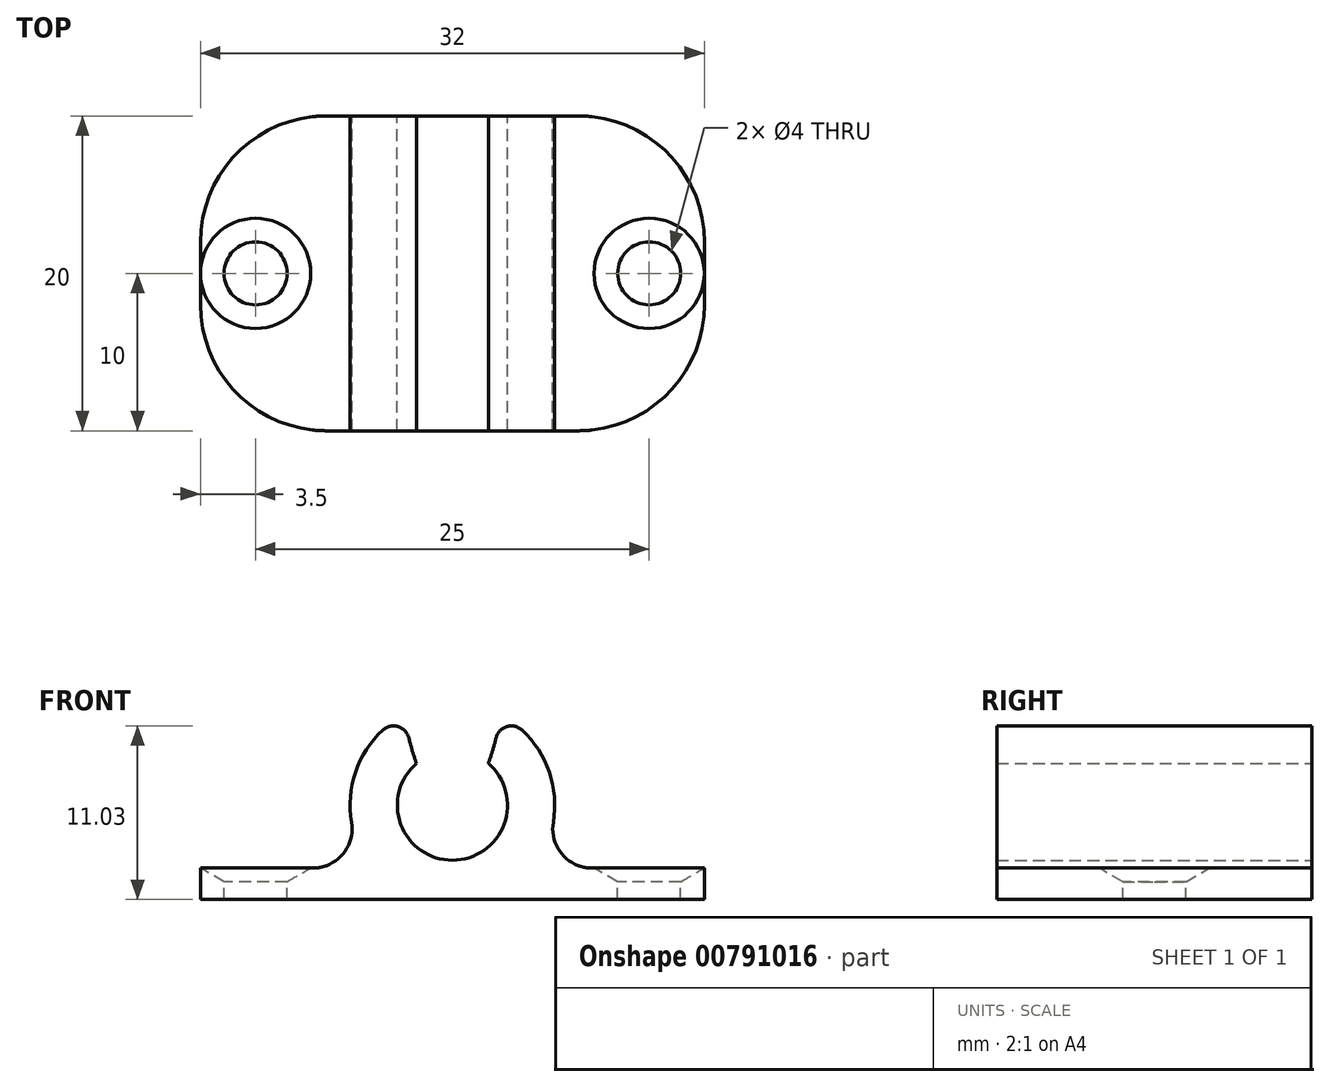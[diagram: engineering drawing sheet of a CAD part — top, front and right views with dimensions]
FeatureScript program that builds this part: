
annotation { "Feature Type Name" : "Feature", "Feature Type Description" : "" }
export const myFeature = defineFeature(function(context is Context, id is Id, definition is map)
    precondition{}
    {
        {
            var Q0;
            Q0=qCreatedBy(makeId("Front.planeOp"),FACE);
            var sketch = newSketch(context, id + "F0", { "sketchPlane" : qUnion([Q0])});
            skLineSegment(sketch, "E0.bottom", {"start": v(-16, 0) * mm, "end": v(16, 0) * mm});
            skLineSegment(sketch, "E0.top", {"start": v(-16, 2) * mm, "end": v(-8.87, 2) * mm});
            skLineSegment(sketch, "E0.left", {"start": v(-16, 0) * mm, "end": v(-16, 2) * mm});
            skLineSegment(sketch, "E0.right", {"start": v(16, 0) * mm, "end": v(16, 2) * mm});
            skArc(sketch, "E1", {"start": v(-2.28, 8.66) * mm, "mid": v(0, 2.5) * mm, "end": v(2.28, 8.66) * mm});
            skArc(sketch, "E2", {"start": v(-3.07, 11.73) * mm, "mid": v(-5.84, 8.86) * mm, "end": v(-6.4, 4.92) * mm});
            skArc(sketch, "E3", {"start": v(6.4, 4.92) * mm, "mid": v(6.96, 2.89) * mm, "end": v(8.87, 2) * mm});
            skArc(sketch, "E4", {"start": v(-8.87, 2) * mm, "mid": v(-6.96, 2.89) * mm, "end": v(-6.4, 4.92) * mm});
            skEllipticalArc(sketch, "E5", {});
            skEllipticalArc(sketch, "E6.trimOffspring", {});
            skArc(sketch, "E7.trimOffspring", {"start": v(6.4, 4.92) * mm, "mid": v(5.84, 8.86) * mm, "end": v(3.07, 11.73) * mm});
            skLineSegment(sketch, "E8.trimOffspring", {"start": v(8.87, 2) * mm, "end": v(16, 2) * mm});
            const initialGuessF0  = {"E5": [0, 0.016997944563627243, 0, -1, 0.010997944563627243, 0.0035, 5.212081421117064, 5.573529930797932], "E6.trimOffspring": [0, 0.016997944563627243, 0, -1, 0.010997944563627243, 0.0035, 0.7096553763816549, 1.0711038860625215]};
            skSetInitialGuess(sketch, initialGuessF0);
            skSolve(sketch);
        }
        {
            var Q0;
            Q0=makeQuery(id+"F0.imprint","IMPRINT",FACE,{"disambiguationData":[TD([[makeQuery(id+"F0.imprint","IMPRINT",EDGE,{"derivedFrom":sQuery(id+"F0.wireOp",EDGE,"E0.bottom")}),1.0]])]});
            extrude(context, id + "F1", {"entities" : qUnion([Q0]), "flatOperationType" : FlatOperationType.REMOVE, "depth" : 20 * mm, "offsetDistance" : 25 * mm, "domain" : OperationDomain.MODEL});
        }
        {
            var Q0;
            Q0=makeQuery(id+"F1.opExtrude","SWEPT_EDGE",EDGE,{"disambiguationData":[OSD([sQuery(id+"F0.wireOp",EDGE,"E2"),sQuery(id+"F0.wireOp",EDGE,"E5")])]});
            var Q1;
            Q1=makeQuery(id+"F1.opExtrude","SWEPT_EDGE",EDGE,{"disambiguationData":[OSD([sQuery(id+"F0.wireOp",EDGE,"E6.trimOffspring"),sQuery(id+"F0.wireOp",EDGE,"E7.trimOffspring")])]});
            fillet(context, id + "F2", {"entities" : qUnion([Q0, Q1]), "radius" : 1 * mm, "tangentPropagation" : true, "allowEdgeOverflow" : false});
        }
        {
            var Q0;
            Q0=makeQuery(id+"F1.opExtrude","CAP_EDGE",EDGE,{"disambiguationData":[OSD([sQuery(id+"F0.wireOp",EDGE,"E0.left")])],"isStart":false});
            var Q1;
            Q1=makeQuery(id+"F1.opExtrude","CAP_EDGE",EDGE,{"disambiguationData":[OSD([sQuery(id+"F0.wireOp",EDGE,"E0.right")])],"isStart":false});
            var Q2;
            Q2=makeQuery(id+"F1.opExtrude","CAP_EDGE",EDGE,{"disambiguationData":[OSD([sQuery(id+"F0.wireOp",EDGE,"E0.right")])],"isStart":true});
            var Q3;
            Q3=makeQuery(id+"F1.opExtrude","CAP_EDGE",EDGE,{"disambiguationData":[OSD([sQuery(id+"F0.wireOp",EDGE,"E0.left")])],"isStart":true});
            fillet(context, id + "F3", {"entities" : qUnion([Q0, Q1, Q2, Q3]), "radius" : 8 * mm, "tangentPropagation" : true, "allowEdgeOverflow" : false});
        }
        {
            var Q0;
            Q0=makeQuery(id+"F1.opExtrude","SWEPT_FACE",FACE,{"disambiguationData":[OSD([sQuery(id+"F0.wireOp",EDGE,"E8.trimOffspring")])]});
            var sketch = newSketch(context, id + "F4", { "sketchPlane" : qUnion([Q0])});
            skPoint(sketch, "E9", {"position": v(-12.5, -10) * mm});
            skPoint(sketch, "E10", {"position": v(12.5, -10) * mm});
            skSolve(sketch);
        }
        {
            var Q0;
            Q0=sQuery(id+"F4.wireOp",VERTEX,"E9");
            var Q1;
            Q1=sQuery(id+"F4.wireOp",VERTEX,"E10");
            var Q2;
            Q2=makeQuery(id+"F1.opExtrude","SWEPT_BODY",BODY,{"disambiguationData":[OSD([sQuery(id+"F0.wireOp",EDGE,"E0.bottom"),sQuery(id+"F0.wireOp",EDGE,"E0.top"),sQuery(id+"F0.wireOp",EDGE,"E0.left"),sQuery(id+"F0.wireOp",EDGE,"E0.right"),sQuery(id+"F0.wireOp",EDGE,"E1"),sQuery(id+"F0.wireOp",EDGE,"E2"),sQuery(id+"F0.wireOp",EDGE,"E3"),sQuery(id+"F0.wireOp",EDGE,"E4"),sQuery(id+"F0.wireOp",EDGE,"E5"),sQuery(id+"F0.wireOp",EDGE,"E6.trimOffspring"),sQuery(id+"F0.wireOp",EDGE,"E7.trimOffspring"),sQuery(id+"F0.wireOp",EDGE,"E8.trimOffspring")])]});
            hole(context, id + "F5", {"style" : HoleStyle.C_SINK, "endStyle" : HoleEndStyle.THROUGH, "holeDiameter" : 4 * mm, "cSinkDiameter" : 7 * mm, "cSinkAngle" : 120 * degree, "majorDiameter" : 5 * mm, "isTappedThrough" : true, "tappedDepth" : 12 * mm, "tapClearance" : 3, "locations" : qUnion([Q0, Q1]), "scope" : qUnion([Q2])});
        }
    });
